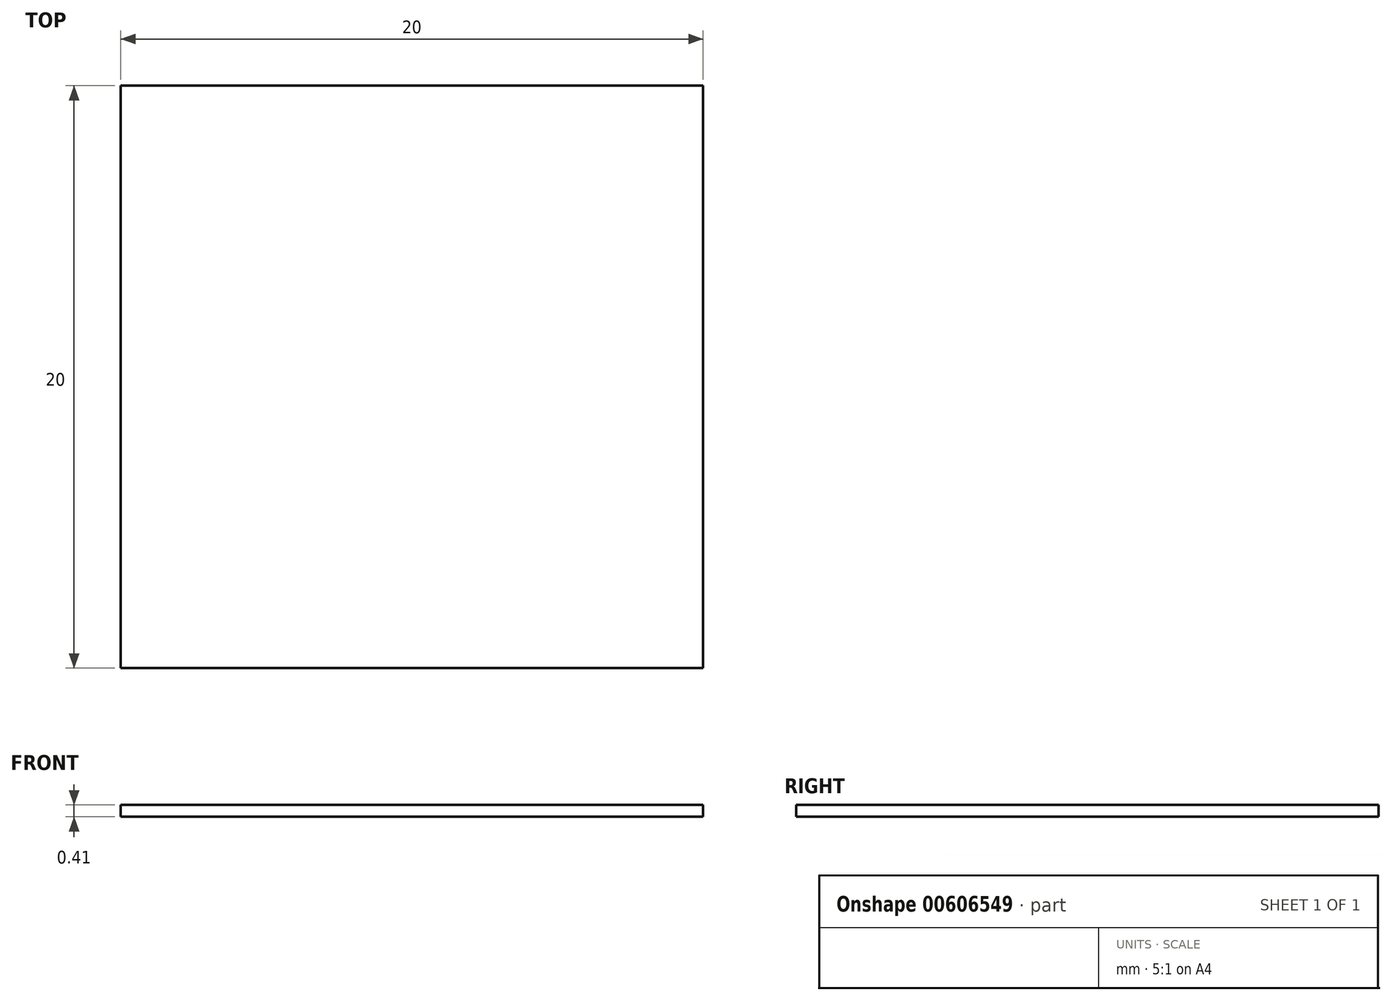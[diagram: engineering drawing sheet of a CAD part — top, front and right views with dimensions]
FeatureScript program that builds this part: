
annotation { "Feature Type Name" : "Feature", "Feature Type Description" : "" }
export const myFeature = defineFeature(function(context is Context, id is Id, definition is map)
    precondition{}
    {
        {
            var Q0;
            Q0=qCreatedBy(makeId("Top.planeOp"),FACE);
            var sketch = newSketch(context, id + "F0", { "sketchPlane" : qUnion([Q0])});
            skLineSegment(sketch, "E0.bottom", {"start": v(10, 10) * mm, "end": v(-10, 10) * mm});
            skLineSegment(sketch, "E0.top", {"start": v(10, -10) * mm, "end": v(-10, -10) * mm});
            skLineSegment(sketch, "E0.left", {"start": v(10, 10) * mm, "end": v(10, -10) * mm});
            skLineSegment(sketch, "E0.right", {"start": v(-10, 10) * mm, "end": v(-10, -10) * mm});
            skPoint(sketch, "E0.middle", {"position": v(0, 0) * mm});
            skSolve(sketch);
        }
        {
            var Q0;
            Q0 = qSketchRegion(id + "F0", true);
            extrude(context, id + "F1", {"entities" : qUnion([Q0]), "depth" : .41 * mm, "offsetDistance" : 25 * mm});
        }
    });
